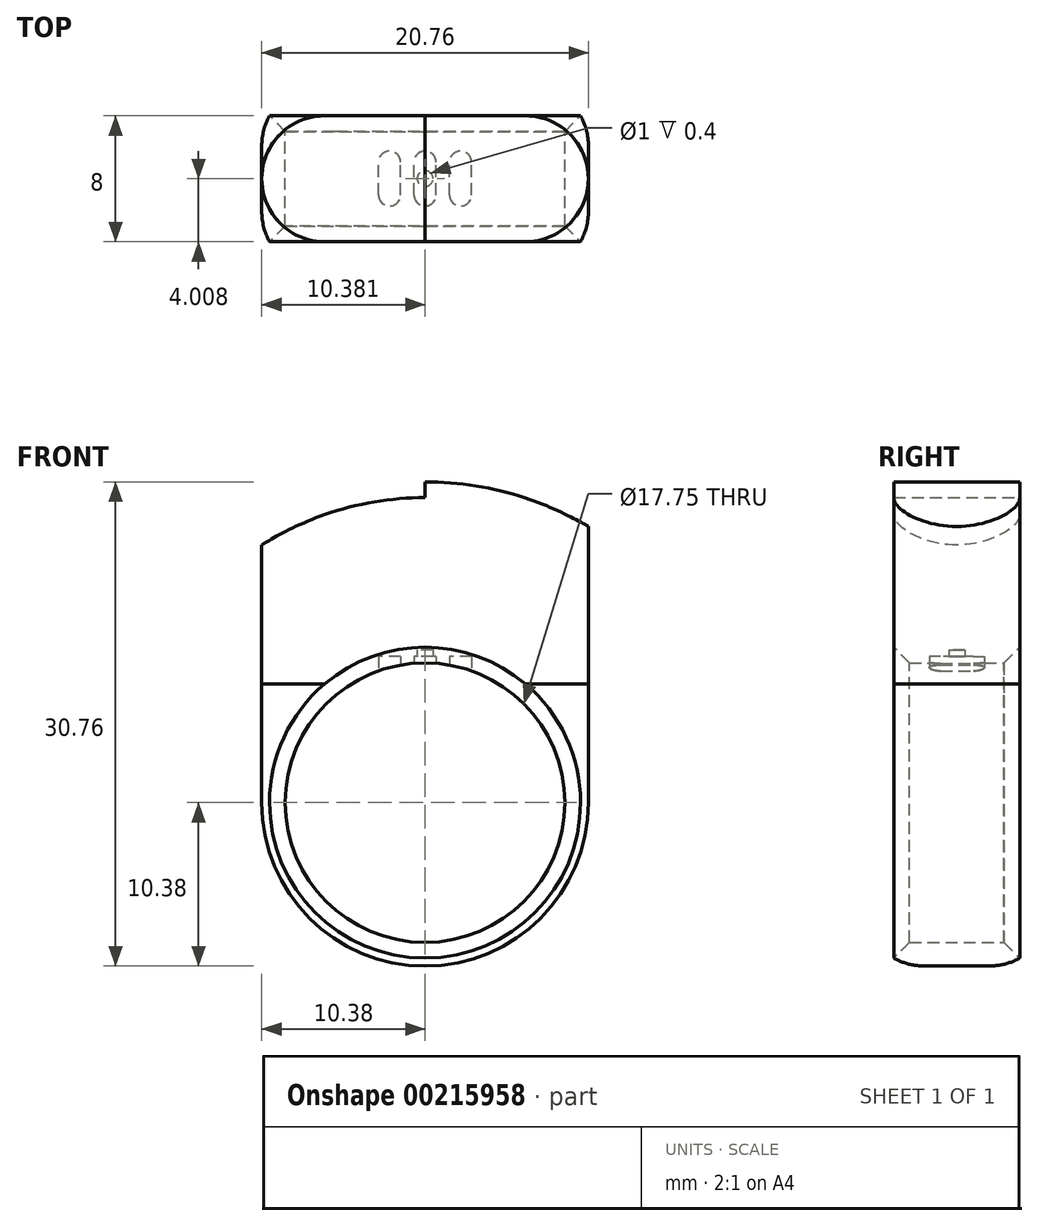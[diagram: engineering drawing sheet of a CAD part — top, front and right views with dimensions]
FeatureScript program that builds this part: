
annotation { "Feature Type Name" : "Feature", "Feature Type Description" : "" }
export const myFeature = defineFeature(function(context is Context, id is Id, definition is map)
    precondition{}
    {
        {
            var Q0;
            Q0=qCreatedBy(makeId("Front.planeOp"),FACE);
            var sketch = newSketch(context, id + "F0", { "sketchPlane" : qUnion([Q0])});
            skCircle(sketch, "E0", {"center": v(0, 0) * mm, "radius": 8.88 * mm});
            skCircle(sketch, "E1.0", {"center": v(0, 0) * mm, "radius": 10.38 * mm});
            skCircle(sketch, "E2.0", {"center": v(0, 0) * mm, "radius": 20.38 * mm});
            skLineSegment(sketch, "E3", {"start": v(10.38, 0) * mm, "end": v(10.38, 17.54) * mm});
            skLineSegment(sketch, "E4.MirrorCS", {"start": v(-10.38, 0) * mm, "end": v(-10.38, 17.54) * mm});
            skCircle(sketch, "E5.0", {"center": v(0, 0) * mm, "radius": 19.38 * mm});
            skLineSegment(sketch, "E6", {"start": v(-0.5, 20.37) * mm, "end": v(-0.5, 19.37) * mm});
            skLineSegment(sketch, "E7.MirrorCS", {"start": v(0.5, 20.37) * mm, "end": v(0.5, 19.37) * mm});
            skLineSegment(sketch, "E8", {"start": v(0, 20.38) * mm, "end": v(0, 19.38) * mm});
            skArc(sketch, "E9", {"start": v(10.37, 13.23) * mm, "mid": v(0, 16.81) * mm, "end": v(-10.37, 13.23) * mm});
            skLineSegment(sketch, "E10", {"start": v(0, 19.38) * mm, "end": v(0, 16.81) * mm});
            skSolve(sketch);
        }
        {
            var Q0;
            Q0=makeQuery(id+"F0.imprint","IMPRINT",FACE,{"disambiguationData":[TD([[makeQuery(id+"F0.imprint","IMPRINT",EDGE,{"derivedFrom":sQuery(id+"F0.wireOp",EDGE,"E0")}),-1.0]])]});
            extrude(context, id + "F1", {"entities" : qUnion([Q0]), "depth" : 4 * mm, "hasSecondDirection" : true, "secondDirectionOppositeDirection" : true, "secondDirectionDepth" : 4 * mm});
        }
        {
            var Q0;
            Q0=makeQuery(id+"F1.opExtrude","CAP_EDGE",EDGE,{"disambiguationData":[OSD([sQuery(id+"F0.wireOp",EDGE,"E0")])],"isStart":false});
            var Q1;
            Q1=makeQuery(id+"F1.opExtrude","CAP_EDGE",EDGE,{"disambiguationData":[OSD([sQuery(id+"F0.wireOp",EDGE,"E0")])],"isStart":true});
            chamfer(context, id + "F2", {"entities" : qUnion([Q0, Q1]), "width" : 1 * mm, "tangentPropagation" : true});
        }
        {
            var Q0;
            {var subQ0=sQuery(id+"F0.wireOp",EDGE,"E3");var subQ1=sQuery(id+"F0.wireOp",EDGE,"E1.0");var subQ2=makeQuery(id+"F0.imprint","INTERSECT",VERTEX,{"derivedFrom":[subQ1,subQ0]});Q0=makeQuery(id+"F0.imprint","IMPRINT",FACE,{"disambiguationData":[TD([[makeQuery(id+"F0.imprint","IMPRINT",EDGE,{"disambiguationData":[TD([[subQ2,-1.0]])],"derivedFrom":subQ1}),-1.0]])]});}
            var Q1;
            {var subQ0=sQuery(id+"F0.wireOp",EDGE,"E3");var subQ1=sQuery(id+"F0.wireOp",EDGE,"E2.0");var subQ2=makeQuery(id+"F0.imprint","INTERSECT",VERTEX,{"derivedFrom":[subQ1,subQ0]});Q1=makeQuery(id+"F0.imprint","IMPRINT",FACE,{"disambiguationData":[TD([[makeQuery(id+"F0.imprint","IMPRINT",EDGE,{"disambiguationData":[TD([[subQ2,-1.0]])],"derivedFrom":subQ1}),1.0]])]});}
            var Q2;
            {var subQ0=sQuery(id+"F0.wireOp",EDGE,"E7.MirrorCS");Q2=makeQuery(id+"F0.imprint","IMPRINT",FACE,{"disambiguationData":[TD([[makeQuery(id+"F0.imprint","IMPRINT",EDGE,{"derivedFrom":subQ0}),-1.0]])]});}
            var Q3;
            {var subQ3=sQuery(id+"F0.wireOp",EDGE,"E10");Q3=makeQuery(id+"F0.imprint","IMPRINT",FACE,{"disambiguationData":[TD([[makeQuery(id+"F0.imprint","IMPRINT",EDGE,{"derivedFrom":subQ3}),1.0]])]});}
            var Q4;
            {var subQ3=sQuery(id+"F0.wireOp",EDGE,"E10");Q4=makeQuery(id+"F0.imprint","IMPRINT",FACE,{"disambiguationData":[TD([[makeQuery(id+"F0.imprint","IMPRINT",EDGE,{"derivedFrom":subQ3}),-1.0]])]});}
            extrude(context, id + "F3", {"entities" : qUnion([Q0, Q1, Q2, Q3, Q4]), "operationType" : NewBodyOperationType.ADD, "depth" : 4 * mm, "hasSecondDirection" : true, "secondDirectionOppositeDirection" : true, "secondDirectionDepth" : 4 * mm});
        }
        {
            var Q0;
            Q0=makeQuery(id+"F3.opExtrude","CAP_EDGE",EDGE,{"disambiguationData":[OSD([sQuery(id+"F0.wireOp",EDGE,"E3")])],"isStart":false});
            var Q1;
            Q1=makeQuery(id+"F3.opExtrude","CAP_EDGE",EDGE,{"disambiguationData":[OSD([sQuery(id+"F0.wireOp",EDGE,"E3")])],"isStart":true});
            var Q2;
            Q2=makeQuery(id+"F3.opExtrude","CAP_EDGE",EDGE,{"disambiguationData":[OSD([sQuery(id+"F0.wireOp",EDGE,"E4.MirrorCS")])],"isStart":false});
            var Q3;
            Q3=makeQuery(id+"F3.opExtrude","CAP_EDGE",EDGE,{"disambiguationData":[OSD([sQuery(id+"F0.wireOp",EDGE,"E4.MirrorCS")])],"isStart":true});
            fillet(context, id + "F4", {"entities" : qUnion([Q0, Q1, Q2, Q3]), "radius" : 4 * mm, "tangentPropagation" : true, "allowEdgeOverflow" : false});
        }
        {
            var Q0;
            Q0=qCreatedBy(makeId("Top.planeOp"),FACE);
            var sketch = newSketch(context, id + "F5", { "sketchPlane" : qUnion([Q0])});
            skLineSegment(sketch, "E11.bottom", {"start": v(-0.7, 1.06) * mm, "end": v(-0.7, -1.03) * mm});
            skArc(sketch, "E12.filletArc", {"start": v(0.7, 1.06) * mm, "mid": v(0.5, 1.55) * mm, "end": v(0, 1.76) * mm});
            skArc(sketch, "E13.filletArc", {"start": v(0, 1.76) * mm, "mid": v(-0.5, 1.55) * mm, "end": v(-0.7, 1.06) * mm});
            skArc(sketch, "E14.filletArc", {"start": v(0, -1.73) * mm, "mid": v(0.5, -1.53) * mm, "end": v(0.7, -1.03) * mm});
            skArc(sketch, "E15.filletArc", {"start": v(-0.7, -1.03) * mm, "mid": v(-0.5, -1.53) * mm, "end": v(0, -1.73) * mm});
            skLineSegment(sketch, "E16.bottom", {"start": v(-2.95, 1.06) * mm, "end": v(-2.95, -1.03) * mm});
            skLineSegment(sketch, "E16.top", {"start": v(-1.55, 1.06) * mm, "end": v(-1.55, -1.03) * mm});
            skArc(sketch, "E17.filletArc", {"start": v(-1.55, 1.06) * mm, "mid": v(-1.76, 1.55) * mm, "end": v(-2.25, 1.76) * mm});
            skArc(sketch, "E18.filletArc", {"start": v(-2.25, 1.76) * mm, "mid": v(-2.74, 1.55) * mm, "end": v(-2.95, 1.06) * mm});
            skArc(sketch, "E19.filletArc", {"start": v(-2.25, -1.73) * mm, "mid": v(-1.76, -1.53) * mm, "end": v(-1.55, -1.03) * mm});
            skArc(sketch, "E20.filletArc", {"start": v(-2.95, -1.03) * mm, "mid": v(-2.74, -1.53) * mm, "end": v(-2.25, -1.73) * mm});
            skLineSegment(sketch, "E21", {"start": v(0.7, 1.06) * mm, "end": v(0.7, -1.03) * mm});
            skCircle(sketch, "E22", {"center": v(0, 0) * mm, "radius": 0.5 * mm});
            skLineSegment(sketch, "E23.bottom", {"start": v(1.56, 1.06) * mm, "end": v(1.56, -1.03) * mm});
            skLineSegment(sketch, "E23.top", {"start": v(2.96, 1.06) * mm, "end": v(2.96, -1.03) * mm});
            skArc(sketch, "E24.filletArc", {"start": v(2.96, 1.06) * mm, "mid": v(2.75, 1.55) * mm, "end": v(2.26, 1.76) * mm});
            skArc(sketch, "E25.filletArc", {"start": v(2.26, 1.76) * mm, "mid": v(1.76, 1.55) * mm, "end": v(1.56, 1.06) * mm});
            skArc(sketch, "E26.filletArc", {"start": v(2.26, -1.73) * mm, "mid": v(2.75, -1.53) * mm, "end": v(2.96, -1.03) * mm});
            skArc(sketch, "E27.filletArc", {"start": v(1.56, -1.03) * mm, "mid": v(1.76, -1.53) * mm, "end": v(2.26, -1.73) * mm});
            skSolve(sketch);
        }
        {
            var Q0;
            Q0=makeQuery(id+"F5.imprint","IMPRINT",FACE,{"disambiguationData":[TD([[makeQuery(id+"F5.imprint","IMPRINT",EDGE,{"derivedFrom":sQuery(id+"F5.wireOp",EDGE,"E23.bottom")}),1.0]])]});
            var Q1;
            Q1=makeQuery(id+"F5.imprint","IMPRINT",FACE,{"disambiguationData":[TD([[makeQuery(id+"F5.imprint","IMPRINT",EDGE,{"derivedFrom":sQuery(id+"F5.wireOp",EDGE,"E11.bottom")}),1.0]])]});
            var Q2;
            Q2=makeQuery(id+"F5.imprint","IMPRINT",FACE,{"disambiguationData":[TD([[makeQuery(id+"F5.imprint","IMPRINT",EDGE,{"derivedFrom":sQuery(id+"F5.wireOp",EDGE,"E16.bottom")}),1.0]])]});
            extrude(context, id + "F6", {"entities" : qUnion([Q0, Q1, Q2]), "operationType" : NewBodyOperationType.REMOVE, "depth" : 9.3 * mm, "offsetDistance" : 25 * mm});
        }
        {
            var Q0;
            Q0=makeQuery(id+"F5.imprint","IMPRINT",FACE,{"disambiguationData":[TD([[makeQuery(id+"F5.imprint","IMPRINT",EDGE,{"derivedFrom":sQuery(id+"F5.wireOp",EDGE,"E22")}),1.0]])]});
            extrude(context, id + "F7", {"entities" : qUnion([Q0]), "operationType" : NewBodyOperationType.REMOVE, "depth" : 9.7 * mm, "offsetDistance" : 25 * mm});
        }
    });
